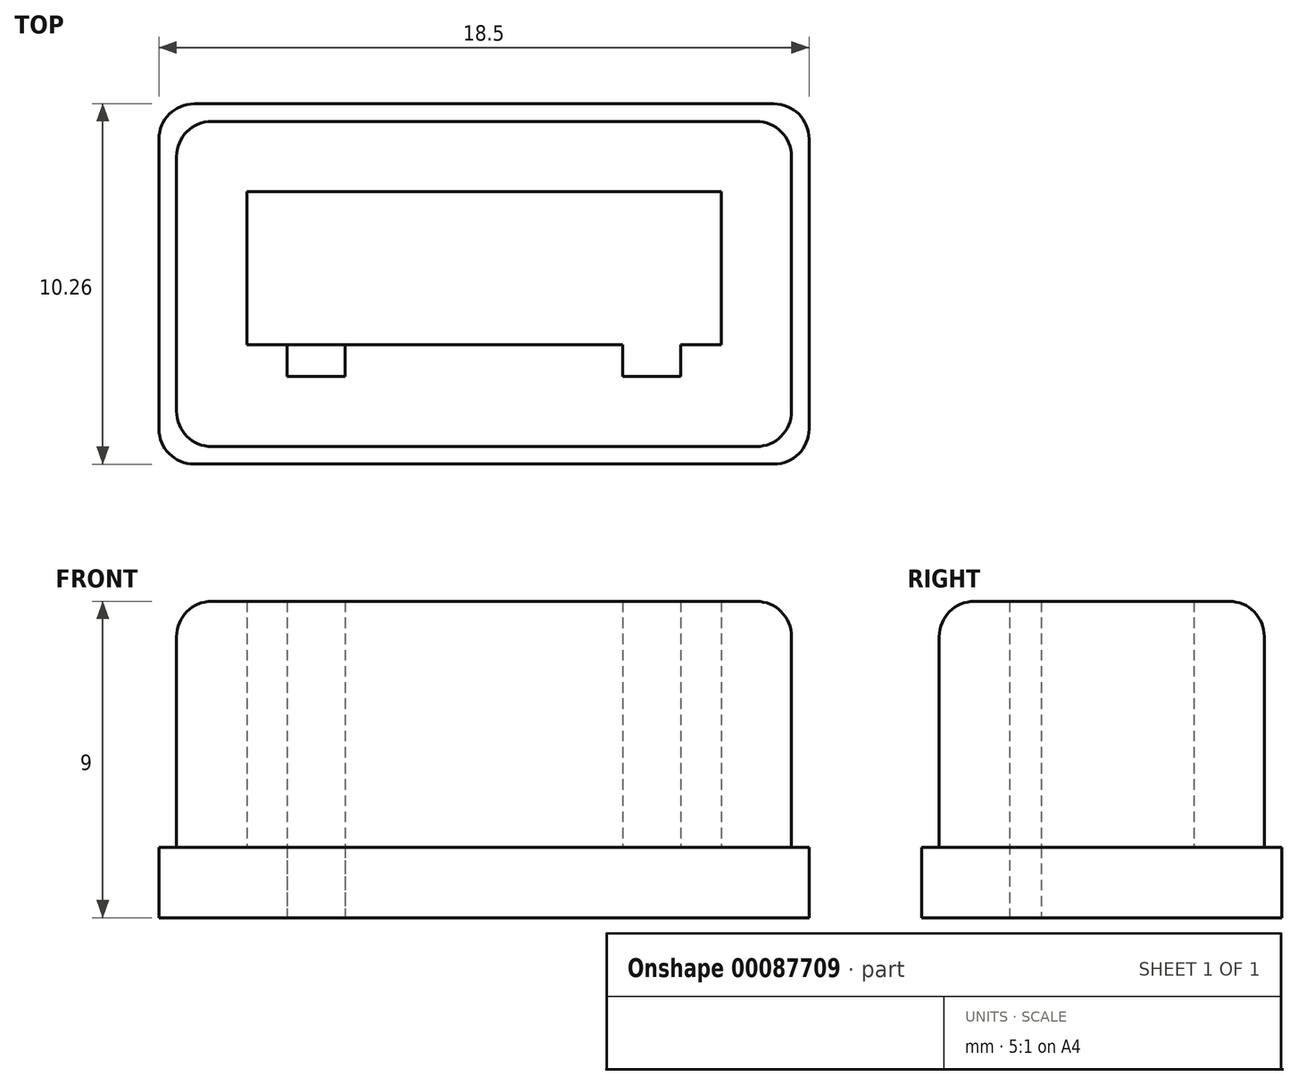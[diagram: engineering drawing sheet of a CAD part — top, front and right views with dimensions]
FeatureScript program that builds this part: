
annotation { "Feature Type Name" : "Feature", "Feature Type Description" : "" }
export const myFeature = defineFeature(function(context is Context, id is Id, definition is map)
    precondition{}
    {
        {
            var Q0;
            Q0=qCreatedBy(makeId("Top.planeOp"),FACE);
            var sketch = newSketch(context, id + "F0", { "sketchPlane" : qUnion([Q0])});
            skLineSegment(sketch, "E0.bottom", {"start": v(6.75, 2.17) * mm, "end": v(-6.75, 2.17) * mm});
            skLineSegment(sketch, "E0.top", {"start": v(6.75, -2.17) * mm, "end": v(-6.75, -2.17) * mm});
            skLineSegment(sketch, "E0.left", {"start": v(6.75, 2.17) * mm, "end": v(6.75, -2.17) * mm});
            skLineSegment(sketch, "E0.right", {"start": v(-6.75, 2.17) * mm, "end": v(-6.75, -2.17) * mm});
            skPoint(sketch, "E0.middle", {"position": v(0, 0) * mm});
            skLineSegment(sketch, "E1.bottom", {"start": v(-5.6, -2.17) * mm, "end": v(-3.95, -2.17) * mm});
            skLineSegment(sketch, "E1.top", {"start": v(-5.6, -3.08) * mm, "end": v(-3.95, -3.08) * mm});
            skLineSegment(sketch, "E1.left", {"start": v(-5.6, -2.17) * mm, "end": v(-5.6, -3.08) * mm});
            skLineSegment(sketch, "E1.right", {"start": v(-3.95, -2.17) * mm, "end": v(-3.95, -3.08) * mm});
            skLineSegment(sketch, "E2.MirrorCS", {"start": v(3.95, -2.17) * mm, "end": v(3.95, -3.08) * mm});
            skLineSegment(sketch, "E3.MirrorCS", {"start": v(5.6, -3.08) * mm, "end": v(3.95, -3.08) * mm});
            skLineSegment(sketch, "E4.MirrorCS", {"start": v(5.6, -2.17) * mm, "end": v(5.6, -3.08) * mm});
            skLineSegment(sketch, "E5.0", {"start": v(-8.75, 4.18) * mm, "end": v(-8.75, -2.17) * mm});
            skLineSegment(sketch, "E5.1", {"start": v(8.75, 4.18) * mm, "end": v(-8.75, 4.18) * mm});
            skLineSegment(sketch, "E5.2", {"start": v(8.75, 4.18) * mm, "end": v(8.75, -2.18) * mm});
            skLineSegment(sketch, "E6.0", {"start": v(5.6, -5.07) * mm, "end": v(3.95, -5.07) * mm});
            skLineSegment(sketch, "E7", {"start": v(8.75, -2.18) * mm, "end": v(8.75, -5.07) * mm});
            skLineSegment(sketch, "E8", {"start": v(5.6, -5.07) * mm, "end": v(8.75, -5.07) * mm});
            skLineSegment(sketch, "E9", {"start": v(3.95, -5.07) * mm, "end": v(-8.75, -5.07) * mm});
            skLineSegment(sketch, "E10", {"start": v(-8.75, -5.07) * mm, "end": v(-8.75, -2.17) * mm});
            skLineSegment(sketch, "E11.0", {"start": v(9.25, 4.68) * mm, "end": v(9.25, -2.18) * mm});
            skLineSegment(sketch, "E11.1", {"start": v(9.25, -2.18) * mm, "end": v(9.25, -5.57) * mm});
            skLineSegment(sketch, "E11.2", {"start": v(9.25, 4.68) * mm, "end": v(-9.25, 4.68) * mm});
            skLineSegment(sketch, "E11.3", {"start": v(5.6, -5.57) * mm, "end": v(9.25, -5.57) * mm});
            skLineSegment(sketch, "E11.4", {"start": v(-9.25, 4.68) * mm, "end": v(-9.25, -2.17) * mm});
            skLineSegment(sketch, "E11.5", {"start": v(-9.25, -5.58) * mm, "end": v(-9.25, -2.17) * mm});
            skLineSegment(sketch, "E11.6", {"start": v(3.95, -5.58) * mm, "end": v(-9.25, -5.58) * mm});
            skLineSegment(sketch, "E11.7", {"start": v(5.6, -5.58) * mm, "end": v(3.95, -5.58) * mm});
            skSolve(sketch);
        }
        {
            var Q0;
            Q0=makeQuery(id+"F0.imprint","IMPRINT",FACE,{"disambiguationData":[TD([[makeQuery(id+"F0.imprint","IMPRINT",EDGE,{"derivedFrom":sQuery(id+"F0.wireOp",EDGE,"E5.0")}),-1.0]])]});
            var Q1;
            Q1=makeQuery(id+"F0.imprint","IMPRINT",FACE,{"disambiguationData":[TD([[makeQuery(id+"F0.imprint","IMPRINT",EDGE,{"derivedFrom":sQuery(id+"F0.wireOp",EDGE,"E0.bottom")}),-1.0]])]});
            var Q2;
            Q2=makeQuery(id+"F0.imprint","IMPRINT",FACE,{"disambiguationData":[TD([[makeQuery(id+"F0.imprint","IMPRINT",EDGE,{"derivedFrom":sQuery(id+"F0.wireOp",EDGE,"E0.bottom")}),1.0]])]});
            var Q3;
            Q3=makeQuery(id+"F0.imprint","IMPRINT",FACE,{"disambiguationData":[TD([[makeQuery(id+"F0.imprint","IMPRINT",EDGE,{"derivedFrom":sQuery(id+"F0.wireOp",EDGE,"E1.bottom")}),-1.0]])]});
            var Q4;
            {var subQ0=sQuery(id+"F0.wireOp",EDGE,"E2.MirrorCS");Q4=makeQuery(id+"F0.imprint","IMPRINT",FACE,{"disambiguationData":[TD([[makeQuery(id+"F0.imprint","IMPRINT",EDGE,{"derivedFrom":subQ0}),1.0]])]});}
            extrude(context, id + "F1", {"entities" : qUnion([Q0, Q1, Q2, Q3, Q4]), "depth" : 2 * mm});
        }
        {
            var Q0;
            Q0=makeQuery(id+"F0.imprint","IMPRINT",FACE,{"disambiguationData":[TD([[makeQuery(id+"F0.imprint","IMPRINT",EDGE,{"derivedFrom":sQuery(id+"F0.wireOp",EDGE,"E0.bottom")}),-1.0]])]});
            extrude(context, id + "F2", {"entities" : qUnion([Q0]), "operationType" : NewBodyOperationType.ADD, "depth" : 9 * mm});
        }
        {
            var Q0;
            Q0=makeQuery(id+"F1.opExtrude","SWEPT_EDGE",EDGE,{"disambiguationData":[OSD([sQuery(id+"F0.wireOp",EDGE,"E11.5"),sQuery(id+"F0.wireOp",EDGE,"E11.6")])]});
            var Q1;
            Q1=makeQuery(id+"F2.opExtrude","SWEPT_EDGE",EDGE,{"disambiguationData":[OSD([sQuery(id+"F0.wireOp",EDGE,"E9"),sQuery(id+"F0.wireOp",EDGE,"E10")])]});
            var Q2;
            Q2=makeQuery(id+"F1.opExtrude","SWEPT_EDGE",EDGE,{"disambiguationData":[OSD([sQuery(id+"F0.wireOp",EDGE,"E11.2"),sQuery(id+"F0.wireOp",EDGE,"E11.4")])]});
            var Q3;
            Q3=makeQuery(id+"F2.opExtrude","SWEPT_EDGE",EDGE,{"disambiguationData":[OSD([sQuery(id+"F0.wireOp",EDGE,"E5.0"),sQuery(id+"F0.wireOp",EDGE,"E5.1")])]});
            var Q4;
            Q4=makeQuery(id+"F2.opExtrude","SWEPT_EDGE",EDGE,{"disambiguationData":[OSD([sQuery(id+"F0.wireOp",EDGE,"E7"),sQuery(id+"F0.wireOp",EDGE,"E8")])]});
            var Q5;
            Q5=makeQuery(id+"F1.opExtrude","SWEPT_EDGE",EDGE,{"disambiguationData":[OSD([sQuery(id+"F0.wireOp",EDGE,"E11.1"),sQuery(id+"F0.wireOp",EDGE,"E11.3")])]});
            var Q6;
            Q6=makeQuery(id+"F2.opExtrude","SWEPT_EDGE",EDGE,{"disambiguationData":[OSD([sQuery(id+"F0.wireOp",EDGE,"E5.1"),sQuery(id+"F0.wireOp",EDGE,"E5.2")])]});
            var Q7;
            Q7=makeQuery(id+"F1.opExtrude","SWEPT_EDGE",EDGE,{"disambiguationData":[OSD([sQuery(id+"F0.wireOp",EDGE,"E11.0"),sQuery(id+"F0.wireOp",EDGE,"E11.2")])]});
            var Q8;
            Q8=makeQuery(id+"F2.opExtrude","CAP_EDGE",EDGE,{"disambiguationData":[OSD([sQuery(id+"F0.wireOp",EDGE,"E6.0"),sQuery(id+"F0.wireOp",EDGE,"E8"),sQuery(id+"F0.wireOp",EDGE,"E9")])],"isStart":false});
            var Q9;
            Q9=makeQuery(id+"F2.opExtrude","CAP_EDGE",EDGE,{"disambiguationData":[OSD([sQuery(id+"F0.wireOp",EDGE,"E5.0"),sQuery(id+"F0.wireOp",EDGE,"E10")])],"isStart":false});
            var Q10;
            Q10=makeQuery(id+"F2.opExtrude","CAP_EDGE",EDGE,{"disambiguationData":[OSD([sQuery(id+"F0.wireOp",EDGE,"E5.1")])],"isStart":false});
            var Q11;
            Q11=makeQuery(id+"F2.opExtrude","CAP_EDGE",EDGE,{"disambiguationData":[OSD([sQuery(id+"F0.wireOp",EDGE,"E5.2"),sQuery(id+"F0.wireOp",EDGE,"E7")])],"isStart":false});
            fillet(context, id + "F3", {"entities" : qUnion([Q0, Q1, Q2, Q3, Q4, Q5, Q6, Q7, Q8, Q9, Q10, Q11]), "radius" : 1 * mm, "tangentPropagation" : true, "allowEdgeOverflow" : false});
        }
    });
